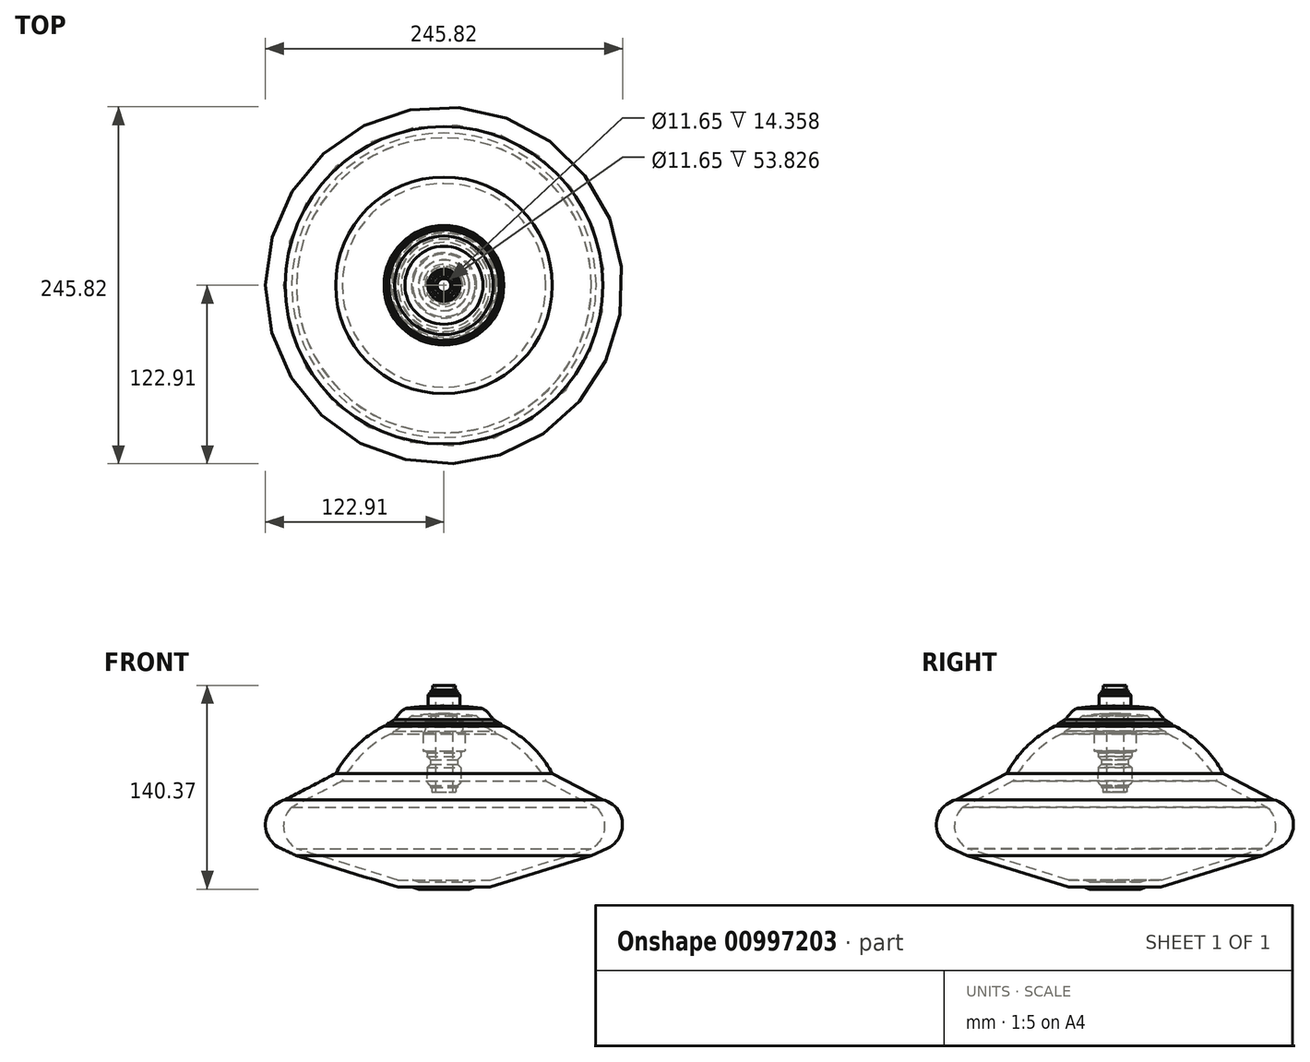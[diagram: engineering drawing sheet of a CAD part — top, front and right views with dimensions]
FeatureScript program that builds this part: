
annotation { "Feature Type Name" : "Feature", "Feature Type Description" : "" }
export const myFeature = defineFeature(function(context is Context, id is Id, definition is map)
    precondition{}
    {
        {
            var Q0;
            Q0=qCreatedBy(makeId("Front.planeOp"),FACE);
            var sketch = newSketch(context, id + "F0", { "sketchPlane" : qUnion([Q0])});
            skLineSegment(sketch, "E0", {"start": v(0, 103.84) * mm, "end": v(4.7, 102.86) * mm});
            skArc(sketch, "E1", {"start": v(26.86, 101.28) * mm, "mid": v(15.8, 102.46) * mm, "end": v(4.7, 102.86) * mm});
            skArc(sketch, "E2", {"start": v(33.96, 93.7) * mm, "mid": v(30.71, 97.77) * mm, "end": v(26.86, 101.28) * mm});
            skLineSegment(sketch, "E3", {"start": v(33.96, 93.7) * mm, "end": v(38.05, 91.06) * mm});
            skLineSegment(sketch, "E4", {"start": v(38.05, 91.06) * mm, "end": v(38.8, 91.06) * mm});
            skLineSegment(sketch, "E5", {"start": v(38.8, 91.06) * mm, "end": v(40.23, 89.1) * mm});
            skLineSegment(sketch, "E6", {"start": v(40.23, 89.1) * mm, "end": v(41.2, 89.1) * mm});
            skLineSegment(sketch, "E7", {"start": v(90.45, -3.46) * mm, "end": v(31.7, -21.72) * mm});
            skLineSegment(sketch, "E8", {"start": v(31.7, -21.72) * mm, "end": v(21.45, -21.72) * mm});
            skLineSegment(sketch, "E9", {"start": v(21.45, -21.72) * mm, "end": v(17.34, -23.16) * mm});
            skLineSegment(sketch, "E10", {"start": v(17.34, -23.16) * mm, "end": v(0, -23.16) * mm});
            skLineSegment(sketch, "E11", {"start": v(0, -23.16) * mm, "end": v(0, -18.2) * mm});
            skLineSegment(sketch, "E12", {"start": v(0, 97.65) * mm, "end": v(0, 108.65) * mm});
            skLineSegment(sketch, "E13", {"start": v(0, 108.65) * mm, "end": v(0, 97.65) * mm});
            skArc(sketch, "E14", {"start": v(74.54, 56.55) * mm, "mid": v(60.38, 75.4) * mm, "end": v(41.2, 89.1) * mm});
            skLineSegment(sketch, "E15", {"start": v(74.54, 56.55) * mm, "end": v(109.27, 38.47) * mm});
            skLineSegment(sketch, "E16", {"start": v(101.6, 0) * mm, "end": v(31.7, -21.72) * mm});
            skLineSegment(sketch, "E17", {"start": v(101.6, 0) * mm, "end": v(112.65, 5.13) * mm});
            skArc(sketch, "E18", {"start": v(112.65, 5.13) * mm, "mid": v(122.82, 23) * mm, "end": v(109.27, 38.47) * mm});
            skLineSegment(sketch, "E19", {"start": v(0, 98.64) * mm, "end": v(0, 97.65) * mm});
            skArc(sketch, "E20", {"start": v(22.42, 96.07) * mm, "mid": v(11.24, 97.26) * mm, "end": v(0, 97.65) * mm});
            skArc(sketch, "E21", {"start": v(29.52, 88.49) * mm, "mid": v(26.27, 92.56) * mm, "end": v(22.42, 96.07) * mm});
            skLineSegment(sketch, "E22", {"start": v(29.52, 88.49) * mm, "end": v(33.61, 85.85) * mm});
            skLineSegment(sketch, "E23", {"start": v(33.61, 85.85) * mm, "end": v(34.36, 85.85) * mm});
            skLineSegment(sketch, "E24", {"start": v(34.36, 85.85) * mm, "end": v(35.79, 83.88) * mm});
            skLineSegment(sketch, "E25", {"start": v(35.79, 83.88) * mm, "end": v(36.76, 83.88) * mm});
            skLineSegment(sketch, "E26", {"start": v(90.7, 1.49) * mm, "end": v(31.95, -16.77) * mm});
            skLineSegment(sketch, "E27", {"start": v(31.95, -16.77) * mm, "end": v(21.71, -16.77) * mm});
            skLineSegment(sketch, "E28", {"start": v(21.71, -16.77) * mm, "end": v(17.6, -18.2) * mm});
            skLineSegment(sketch, "E29", {"start": v(17.6, -18.2) * mm, "end": v(0, -18.2) * mm});
            skPoint(sketch, "E30.endSnap0", {"position": v(-147.7, -9.95) * mm});
            skArc(sketch, "E31", {"start": v(70.1, 51.34) * mm, "mid": v(55.95, 70.19) * mm, "end": v(36.76, 83.88) * mm});
            skLineSegment(sketch, "E32", {"start": v(70.1, 51.34) * mm, "end": v(104.83, 33.26) * mm});
            skLineSegment(sketch, "E33", {"start": v(101.86, 4.95) * mm, "end": v(31.95, -16.77) * mm});
            skLineSegment(sketch, "E34", {"start": v(100.22, 4.2) * mm, "end": v(101.86, 4.95) * mm});
            skArc(sketch, "E35", {"start": v(100.22, 4.2) * mm, "mid": v(110.27, 17.5) * mm, "end": v(104.83, 33.26) * mm});
            skLineSegment(sketch, "E36.trimOffspring", {"start": v(0, -18.2) * mm, "end": v(0, -103.31) * mm});
            skLineSegment(sketch, "E37.trimOffspring", {"start": v(0, 97.65) * mm, "end": v(0, 103.84) * mm});
            skLineSegment(sketch, "E38.trimOffspring", {"start": v(0, 97.65) * mm, "end": v(0, 98.64) * mm});
            skLineSegment(sketch, "E39", {"start": v(0, -18.2) * mm, "end": v(0, 0) * mm});
            skSolve(sketch);
        }
        {
            var Q0;
            Q0=qCreatedBy(makeId("Front.planeOp"),FACE);
            var sketch = newSketch(context, id + "F1", { "sketchPlane" : qUnion([Q0])});
            skLineSegment(sketch, "E40", {"start": v(7.9, 117.21) * mm, "end": v(7.9, 114.06) * mm});
            skLineSegment(sketch, "E41", {"start": v(7.9, 114.06) * mm, "end": v(9, 113.48) * mm});
            skLineSegment(sketch, "E42", {"start": v(9, 113.48) * mm, "end": v(9, 112.28) * mm});
            skArc(sketch, "E43", {"start": v(11, 110.18) * mm, "mid": v(10.24, 111.45) * mm, "end": v(9, 112.28) * mm});
            skLineSegment(sketch, "E44", {"start": v(11, 110.18) * mm, "end": v(11, 104.19) * mm});
            skLineSegment(sketch, "E45", {"start": v(11, 104.19) * mm, "end": v(11, 99.62) * mm});
            skLineSegment(sketch, "E46", {"start": v(11, 99.62) * mm, "end": v(9.94, 98.94) * mm});
            skLineSegment(sketch, "E47", {"start": v(9.94, 98.94) * mm, "end": v(8.9, 98.26) * mm});
            skLineSegment(sketch, "E48", {"start": v(8.9, 98.26) * mm, "end": v(8.9, 92.83) * mm});
            skLineSegment(sketch, "E49", {"start": v(8.9, 92.83) * mm, "end": v(12.96, 92.83) * mm});
            skLineSegment(sketch, "E50", {"start": v(12.96, 92.83) * mm, "end": v(12.96, 86.55) * mm});
            skArc(sketch, "E51", {"start": v(12.96, 86.55) * mm, "mid": v(13.38, 85.42) * mm, "end": v(14.44, 84.84) * mm});
            skLineSegment(sketch, "E52", {"start": v(16.86, 84.84) * mm, "end": v(16.86, 72) * mm});
            skArc(sketch, "E53", {"start": v(13.62, 72) * mm, "mid": v(12.41, 71.62) * mm, "end": v(11.62, 70.64) * mm});
            skLineSegment(sketch, "E54", {"start": v(11.62, 70.64) * mm, "end": v(11.62, 68.22) * mm});
            skLineSegment(sketch, "E55", {"start": v(11.62, 68.22) * mm, "end": v(9.26, 66.16) * mm});
            skLineSegment(sketch, "E56", {"start": v(9.26, 66.16) * mm, "end": v(9.26, 62.68) * mm});
            skLineSegment(sketch, "E57", {"start": v(9.26, 62.68) * mm, "end": v(11.62, 60.5) * mm});
            skLineSegment(sketch, "E58", {"start": v(11.62, 60.5) * mm, "end": v(11.77, 51.37) * mm});
            skArc(sketch, "E59", {"start": v(9.25, 48.37) * mm, "mid": v(10.9, 49.55) * mm, "end": v(11.77, 51.37) * mm});
            skLineSegment(sketch, "E60", {"start": v(9.25, 48.37) * mm, "end": v(9.25, 46.89) * mm});
            skLineSegment(sketch, "E61", {"start": v(9.25, 46.89) * mm, "end": v(8.25, 46.89) * mm});
            skLineSegment(sketch, "E62", {"start": v(8.25, 46.89) * mm, "end": v(8.25, 43.72) * mm});
            skLineSegment(sketch, "E63", {"start": v(0, 27.97) * mm, "end": v(0, 101.46) * mm});
            skLineSegment(sketch, "E64", {"start": v(14.44, 84.84) * mm, "end": v(14.44, 72) * mm});
            skLineSegment(sketch, "E65", {"start": v(14.44, 72) * mm, "end": v(13.62, 72) * mm});
            skLineSegment(sketch, "E66", {"start": v(7.9, 117.21) * mm, "end": v(5.82, 117.21) * mm});
            skLineSegment(sketch, "E67", {"start": v(5.82, 117.21) * mm, "end": v(5.82, 43.72) * mm});
            skLineSegment(sketch, "E68", {"start": v(5.82, 43.72) * mm, "end": v(8.25, 43.72) * mm});
            skSolve(sketch);
        }
        {
            var Q0;
            Q0 = qSketchRegion(id + "F1", true);
            var Q1;
            Q1=sQuery(id+"F1.wireOp",EDGE,"E63");
            revolve(context, id + "F2", {"surfaceOperationType" : NewSurfaceOperationType.NEW, "entities" : qUnion([Q0]), "axis" : qUnion([Q1]), "revolveType" : RevolveType.FULL});
        }
        {
            var Q0;
            Q0 = qSketchRegion(id + "F0", true);
            var Q1;
            Q1=sQuery(id+"F1.wireOp",EDGE,"E63");
            revolve(context, id + "F3", {"operationType" : NewBodyOperationType.ADD, "surfaceOperationType" : NewSurfaceOperationType.NEW, "entities" : qUnion([Q0]), "axis" : qUnion([Q1]), "revolveType" : RevolveType.FULL});
        }
    });
